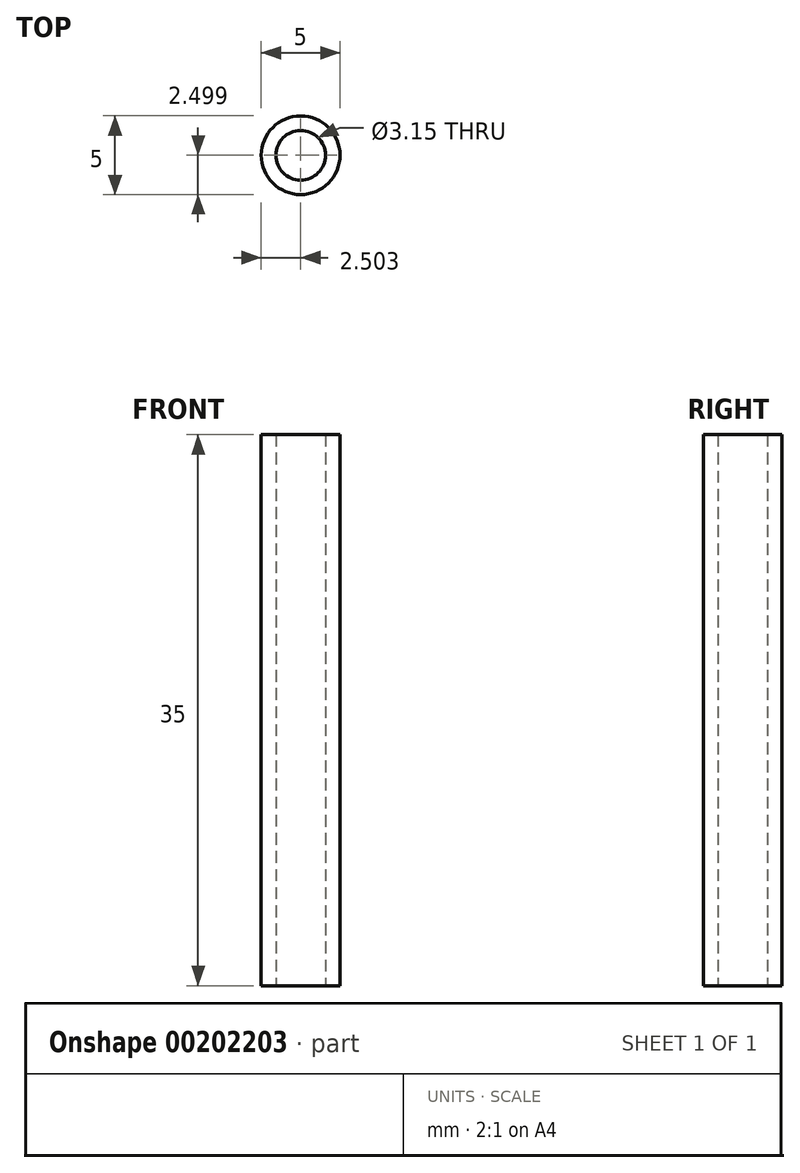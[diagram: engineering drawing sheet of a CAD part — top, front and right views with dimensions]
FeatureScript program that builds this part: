
annotation { "Feature Type Name" : "Feature", "Feature Type Description" : "" }
export const myFeature = defineFeature(function(context is Context, id is Id, definition is map)
    precondition{}
    {
        {
            var Q0;
            Q0=qCreatedBy(makeId("Top.planeOp"),FACE);
            var sketch = newSketch(context, id + "F0", { "sketchPlane" : qUnion([Q0])});
            skCircle(sketch, "E0", {"center": v(-51.02, 31.59) * mm, "radius": 2.5 * mm});
            skCircle(sketch, "E1", {"center": v(-51.02, 31.59) * mm, "radius": 1.57 * mm});
            skSolve(sketch);
        }
        {
            var Q0;
            Q0=qSketchRegion(id+"F0",true);
            extrude(context, id + "F1", {"entities" : qUnion([Q0]), "depth" : 35 * mm});
        }
    });
